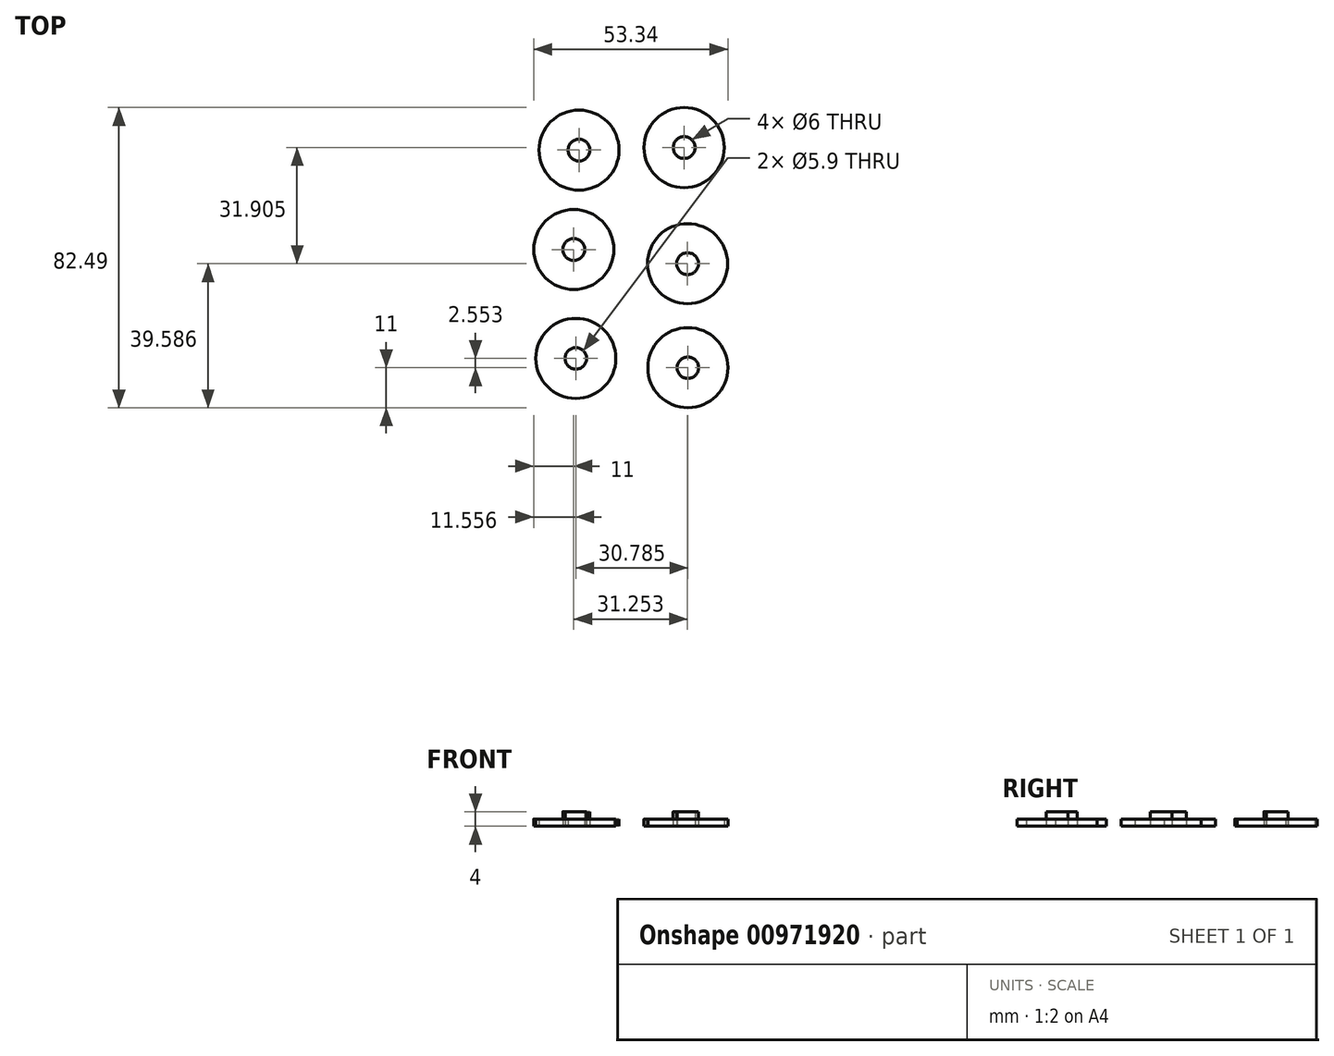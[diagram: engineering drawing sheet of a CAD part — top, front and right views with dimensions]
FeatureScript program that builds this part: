
annotation { "Feature Type Name" : "Feature", "Feature Type Description" : "" }
export const myFeature = defineFeature(function(context is Context, id is Id, definition is map)
    precondition{}
    {
        {
            var Q0;
            Q0=qCreatedBy(makeId("Top.planeOp"),FACE);
            var sketch = newSketch(context, id + "F0", { "sketchPlane" : qUnion([Q0])});
            skCircle(sketch, "E0", {"center": v(-16.36, 18.73) * mm, "radius": 11 * mm});
            skCircle(sketch, "E1", {"center": v(-16.36, 18.73) * mm, "radius": 3 * mm});
            skCircle(sketch, "E2", {"center": v(12.51, 19.41) * mm, "radius": 11 * mm});
            skCircle(sketch, "E3", {"center": v(12.51, 19.41) * mm, "radius": 3 * mm});
            skCircle(sketch, "E4", {"center": v(-17.8, -8.6) * mm, "radius": 11 * mm});
            skCircle(sketch, "E5", {"center": v(-17.8, -8.6) * mm, "radius": 3 * mm});
            skCircle(sketch, "E6", {"center": v(13.45, -12.5) * mm, "radius": 11 * mm});
            skCircle(sketch, "E7", {"center": v(13.45, -12.5) * mm, "radius": 3 * mm});
            skCircle(sketch, "E8", {"center": v(-17.24, -38.53) * mm, "radius": 11 * mm});
            skCircle(sketch, "E9", {"center": v(-17.24, -38.53) * mm, "radius": 2.95 * mm});
            skCircle(sketch, "E10", {"center": v(13.54, -41.08) * mm, "radius": 11 * mm});
            skCircle(sketch, "E11", {"center": v(13.54, -41.08) * mm, "radius": 2.95 * mm});
            skSolve(sketch);
        }
        {
            var Q0;
            Q0=makeQuery(id+"F0.imprint","IMPRINT",FACE,{"disambiguationData":[TD([[makeQuery(id+"F0.imprint","IMPRINT",EDGE,{"derivedFrom":sQuery(id+"F0.wireOp",EDGE,"E0")}),1.0]])]});
            var Q1;
            Q1=makeQuery(id+"F0.imprint","IMPRINT",FACE,{"disambiguationData":[TD([[makeQuery(id+"F0.imprint","IMPRINT",EDGE,{"derivedFrom":sQuery(id+"F0.wireOp",EDGE,"E2")}),1.0]])]});
            var Q2;
            Q2=makeQuery(id+"F0.imprint","IMPRINT",FACE,{"disambiguationData":[TD([[makeQuery(id+"F0.imprint","IMPRINT",EDGE,{"derivedFrom":sQuery(id+"F0.wireOp",EDGE,"E4")}),1.0]])]});
            var Q3;
            Q3=makeQuery(id+"F0.imprint","IMPRINT",FACE,{"disambiguationData":[TD([[makeQuery(id+"F0.imprint","IMPRINT",EDGE,{"derivedFrom":sQuery(id+"F0.wireOp",EDGE,"E6")}),1.0]])]});
            var Q4;
            Q4=makeQuery(id+"F0.imprint","IMPRINT",FACE,{"disambiguationData":[TD([[makeQuery(id+"F0.imprint","IMPRINT",EDGE,{"derivedFrom":sQuery(id+"F0.wireOp",EDGE,"E8")}),1.0]])]});
            var Q5;
            Q5=makeQuery(id+"F0.imprint","IMPRINT",FACE,{"disambiguationData":[TD([[makeQuery(id+"F0.imprint","IMPRINT",EDGE,{"derivedFrom":sQuery(id+"F0.wireOp",EDGE,"E10")}),1.0]])]});
            extrude(context, id + "F1", {"entities" : qUnion([Q0, Q1, Q2, Q3, Q4, Q5]), "depth" : 2 * mm, "offsetDistance" : 25 * mm});
        }
        {
            var Q0;
            Q0=makeQuery(id+"F0.imprint","IMPRINT",FACE,{"disambiguationData":[TD([[makeQuery(id+"F0.imprint","IMPRINT",EDGE,{"derivedFrom":sQuery(id+"F0.wireOp",EDGE,"E1")}),1.0]])]});
            var Q1;
            Q1=makeQuery(id+"F0.imprint","IMPRINT",FACE,{"disambiguationData":[TD([[makeQuery(id+"F0.imprint","IMPRINT",EDGE,{"derivedFrom":sQuery(id+"F0.wireOp",EDGE,"E3")}),1.0]])]});
            var Q2;
            Q2=makeQuery(id+"F0.imprint","IMPRINT",FACE,{"disambiguationData":[TD([[makeQuery(id+"F0.imprint","IMPRINT",EDGE,{"derivedFrom":sQuery(id+"F0.wireOp",EDGE,"E5")}),1.0]])]});
            var Q3;
            Q3=makeQuery(id+"F0.imprint","IMPRINT",FACE,{"disambiguationData":[TD([[makeQuery(id+"F0.imprint","IMPRINT",EDGE,{"derivedFrom":sQuery(id+"F0.wireOp",EDGE,"E7")}),1.0]])]});
            var Q4;
            Q4=makeQuery(id+"F0.imprint","IMPRINT",FACE,{"disambiguationData":[TD([[makeQuery(id+"F0.imprint","IMPRINT",EDGE,{"derivedFrom":sQuery(id+"F0.wireOp",EDGE,"E9")}),1.0]])]});
            var Q5;
            Q5=makeQuery(id+"F0.imprint","IMPRINT",FACE,{"disambiguationData":[TD([[makeQuery(id+"F0.imprint","IMPRINT",EDGE,{"derivedFrom":sQuery(id+"F0.wireOp",EDGE,"E11")}),1.0]])]});
            extrude(context, id + "F2", {"entities" : qUnion([Q0, Q1, Q2, Q3, Q4, Q5]), "depth" : 4 * mm, "offsetDistance" : 25 * mm});
        }
    });
